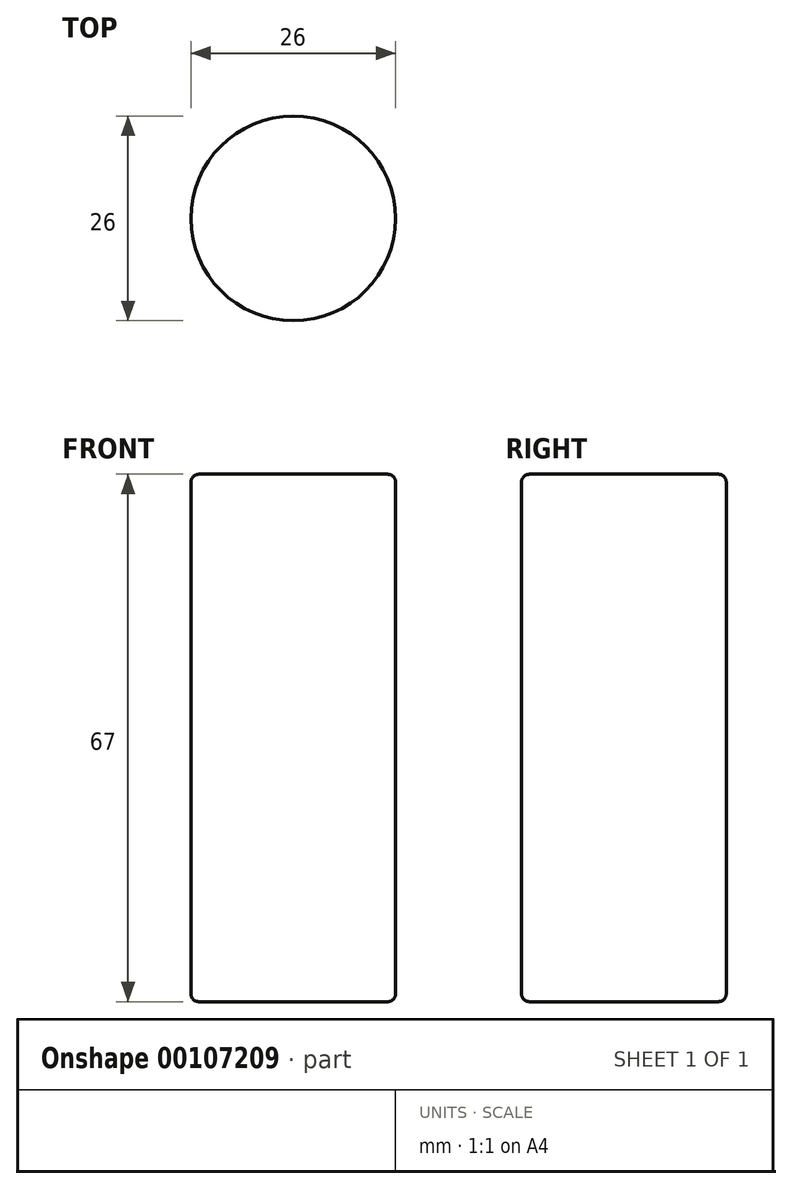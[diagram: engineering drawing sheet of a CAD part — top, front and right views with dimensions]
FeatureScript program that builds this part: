
annotation { "Feature Type Name" : "Feature", "Feature Type Description" : "" }
export const myFeature = defineFeature(function(context is Context, id is Id, definition is map)
    precondition{}
    {
        {
            var Q0;
            Q0=qCreatedBy(makeId("Top.planeOp"),FACE);
            var sketch = newSketch(context, id + "F0", { "sketchPlane" : qUnion([Q0])});
            skCircle(sketch, "E0", {"center": v(0, 0) * mm, "radius": 13 * mm});
            skSolve(sketch);
        }
        {
            var Q0;
            Q0=makeQuery(id+"F0.imprint","IMPRINT",FACE,{"disambiguationData":[TD([[makeQuery(id+"F0.imprint","IMPRINT",EDGE,{"derivedFrom":sQuery(id+"F0.wireOp",EDGE,"E0")}),1.0]])]});
            extrude(context, id + "F1", {"entities" : qUnion([Q0]), "depth" : 67 * mm});
        }
        {
            var Q0;
            Q0=makeQuery(id+"F1.opExtrude","CAP_FACE",FACE,{"disambiguationData":[OSD([sQuery(id+"F0.wireOp",EDGE,"E0")])],"isStart":false});
            var Q1;
            Q1=makeQuery(id+"F1.opExtrude","CAP_FACE",FACE,{"disambiguationData":[OSD([sQuery(id+"F0.wireOp",EDGE,"E0")])],"isStart":true});
            fillet(context, id + "F2", {"entities" : qUnion([Q0, Q1]), "radius" : 1 * mm, "tangentPropagation" : true, "allowEdgeOverflow" : false});
        }
    });
